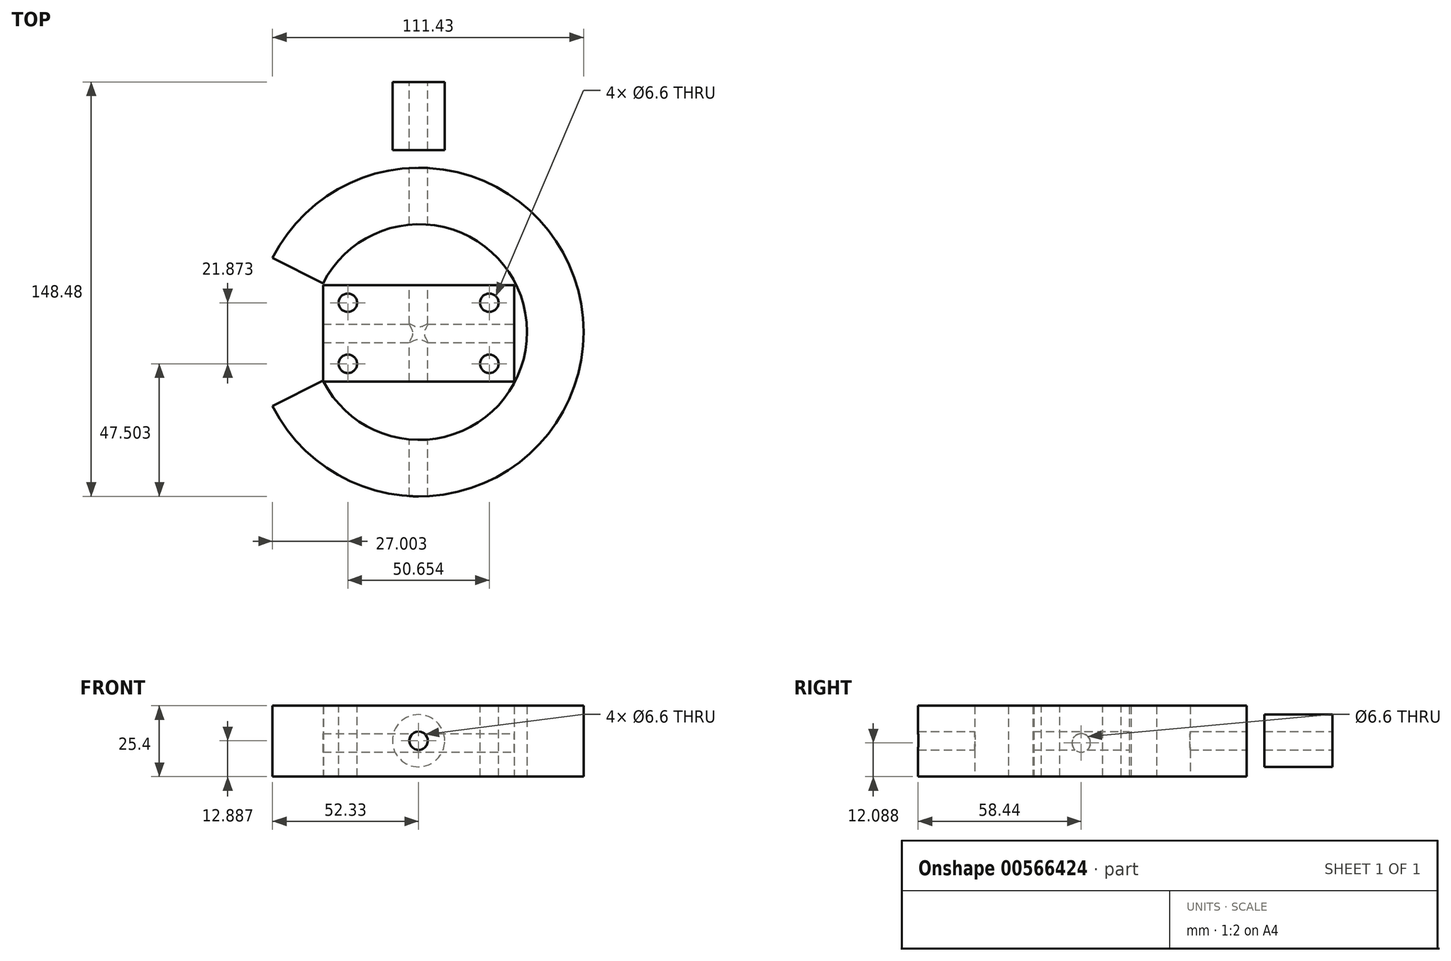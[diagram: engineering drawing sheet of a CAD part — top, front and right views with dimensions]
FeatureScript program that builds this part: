
annotation { "Feature Type Name" : "Feature", "Feature Type Description" : "" }
export const myFeature = defineFeature(function(context is Context, id is Id, definition is map)
    precondition{}
    {
        {
            var Q0;
            Q0=qCreatedBy(makeId("Top.planeOp"),FACE);
            var sketch = newSketch(context, id + "F0", { "sketchPlane" : qUnion([Q0])});
            skLineSegment(sketch, "E0.bottom", {"start": v(-34.25, 17.27) * mm, "end": v(34.25, 17.27) * mm});
            skLineSegment(sketch, "E0.top", {"start": v(-34.25, -17.27) * mm, "end": v(34.25, -17.27) * mm});
            skLineSegment(sketch, "E0.left", {"start": v(-34.25, 17.27) * mm, "end": v(-34.25, -17.27) * mm});
            skLineSegment(sketch, "E0.right", {"start": v(34.25, 17.27) * mm, "end": v(34.25, -17.27) * mm});
            skPoint(sketch, "E0.middle", {"position": v(0, 0) * mm});
            skSolve(sketch);
        }
        {
            var Q0;
            Q0=makeQuery(id+"F0.imprint","IMPRINT",FACE,{"disambiguationData":[TD([[makeQuery(id+"F0.imprint","IMPRINT",EDGE,{"derivedFrom":sQuery(id+"F0.wireOp",EDGE,"E0.bottom")}),-1.0]])]});
            extrude(context, id + "F1", {"entities" : qUnion([Q0]), "depth" : 25.4 * mm, "offsetDistance" : 25.4 * mm});
        }
        {
            var Q0;
            Q0=makeQuery(id+"F1.opExtrude","CAP_FACE",FACE,{"disambiguationData":[OSD([sQuery(id+"F0.wireOp",EDGE,"E0.bottom"),sQuery(id+"F0.wireOp",EDGE,"E0.top"),sQuery(id+"F0.wireOp",EDGE,"E0.left"),sQuery(id+"F0.wireOp",EDGE,"E0.right")])],"isStart":false});
            var sketch = newSketch(context, id + "F2", { "sketchPlane" : qUnion([Q0])});
            skPoint(sketch, "E1", {"position": v(-25.33, 10.94) * mm});
            skPoint(sketch, "E2.MirrorP", {"position": v(25.33, 10.94) * mm});
            skPoint(sketch, "E3.MirrorP", {"position": v(25.33, -10.94) * mm});
            skPoint(sketch, "E4.MirrorP", {"position": v(-25.33, -10.94) * mm});
            skSolve(sketch);
        }
        {
            var Q0;
            Q0=sQuery(id+"F2.wireOp",VERTEX,"E1");
            var Q1;
            Q1=sQuery(id+"F2.wireOp",VERTEX,"E2.MirrorP");
            var Q2;
            Q2=sQuery(id+"F2.wireOp",VERTEX,"E3.MirrorP");
            var Q3;
            Q3=sQuery(id+"F2.wireOp",VERTEX,"E4.MirrorP");
            var Q4;
            Q4=makeQuery(id+"F1.opExtrude","SWEPT_BODY",BODY,{"disambiguationData":[OSD([sQuery(id+"F0.wireOp",EDGE,"E0.bottom"),sQuery(id+"F0.wireOp",EDGE,"E0.top"),sQuery(id+"F0.wireOp",EDGE,"E0.left"),sQuery(id+"F0.wireOp",EDGE,"E0.right")])]});
            hole(context, id + "F3", {"style" : HoleStyle.SIMPLE, "endStyle" : HoleEndStyle.THROUGH, "standardTappedOrClearance" : lookupTablePath({ "standard" : "ISO", "fit" : "Normal", "size" : "M6", "type" : "Clearance" }), "standardBlindInLast" : lookupTablePath({ "fit" : "Standard", "standard" : "ISO", "size" : "M6", "type" : "Clearance" }), "holeDiameter" : 6.6 * mm, "isTappedThrough" : true, "tappedDepth" : 12.7 * mm, "tapClearance" : 3, "startFromSketch" : true, "locations" : qUnion([Q0, Q1, Q2, Q3]), "scope" : qUnion([Q4])});
        }
        {
            var Q0;
            Q0=makeQuery(id+"F1.opExtrude","SWEPT_FACE",FACE,{"disambiguationData":[OSD([sQuery(id+"F0.wireOp",EDGE,"E0.right")])]});
            var sketch = newSketch(context, id + "F4", { "sketchPlane" : qUnion([Q0])});
            skPoint(sketch, "E5", {"position": v(0, 12.09) * mm});
            skSolve(sketch);
        }
        {
            var Q0;
            Q0=sQuery(id+"F4.wireOp",VERTEX,"E5");
            var Q1;
            Q1=makeQuery(id+"F1.opExtrude","SWEPT_BODY",BODY,{"disambiguationData":[OSD([sQuery(id+"F0.wireOp",EDGE,"E0.bottom"),sQuery(id+"F0.wireOp",EDGE,"E0.top"),sQuery(id+"F0.wireOp",EDGE,"E0.left"),sQuery(id+"F0.wireOp",EDGE,"E0.right")])]});
            hole(context, id + "F5", {"style" : HoleStyle.SIMPLE, "endStyle" : HoleEndStyle.THROUGH, "standardTappedOrClearance" : lookupTablePath({ "standard" : "ISO", "fit" : "Normal", "size" : "M6", "type" : "Clearance" }), "standardBlindInLast" : lookupTablePath({ "fit" : "Standard", "standard" : "ISO", "size" : "M6", "type" : "Clearance" }), "holeDiameter" : 6.6 * mm, "isTappedThrough" : true, "tappedDepth" : 12.7 * mm, "tapClearance" : 3, "startFromSketch" : true, "locations" : qUnion([Q0]), "scope" : qUnion([Q1])});
        }
        {
            var Q0;
            Q0=qCreatedBy(makeId("Top.planeOp"),FACE);
            var sketch = newSketch(context, id + "F6", { "sketchPlane" : qUnion([Q0])});
            skArc(sketch, "E6", {"start": v(-34.25, -16.98) * mm, "mid": v(38.85, 0.43) * mm, "end": v(-34.25, 17.84) * mm});
            skArc(sketch, "E7.0", {"start": v(-52.33, -26.11) * mm, "mid": v(59.1, 0.43) * mm, "end": v(-52.33, 26.97) * mm});
            skLineSegment(sketch, "E8", {"start": v(-52.33, -26.11) * mm, "end": v(-34.25, -16.98) * mm});
            skLineSegment(sketch, "E9", {"start": v(-52.33, 26.97) * mm, "end": v(-34.25, 17.84) * mm});
            skSolve(sketch);
        }
        {
            var Q0;
            Q0=makeQuery(id+"F6.imprint","IMPRINT",FACE,{"disambiguationData":[TD([[makeQuery(id+"F6.imprint","IMPRINT",EDGE,{"derivedFrom":sQuery(id+"F6.wireOp",EDGE,"E6")}),-1.0]])]});
            extrude(context, id + "F7", {"entities" : qUnion([Q0]), "operationType" : NewBodyOperationType.ADD, "depth" : 25.4 * mm, "offsetDistance" : 25.4 * mm});
        }
        {
            var Q0;
            Q0=qCreatedBy(makeId("Right.planeOp"),FACE);
            var sketch = newSketch(context, id + "F8", { "sketchPlane" : qUnion([Q0])});
            skLineSegment(sketch, "E10.bottom", {"start": v(65.6, 22.25) * mm, "end": v(90.04, 22.25) * mm});
            skLineSegment(sketch, "E10.top", {"start": v(65.6, 3.53) * mm, "end": v(90.04, 3.53) * mm});
            skLineSegment(sketch, "E10.left", {"start": v(65.6, 3.53) * mm, "end": v(65.6, 22.25) * mm});
            skLineSegment(sketch, "E10.right", {"start": v(90.04, 3.53) * mm, "end": v(90.04, 22.25) * mm});
            skPoint(sketch, "E10.middle", {"position": v(77.82, 12.89) * mm});
            skLineSegment(sketch, "E11", {"start": v(90.04, 12.89) * mm, "end": v(65.6, 12.89) * mm});
            skSolve(sketch);
        }
        {
            var Q0;
            {var subQ0=sQuery(id+"F8.wireOp",EDGE,"E10.bottom");Q0=makeQuery(id+"F8.imprint","IMPRINT",FACE,{"disambiguationData":[TD([[makeQuery(id+"F8.imprint","IMPRINT",EDGE,{"derivedFrom":subQ0}),-1.0]])]});}
            var Q1;
            Q1=sQuery(id+"F8.wireOp",EDGE,"E11");
            revolve(context, id + "F9", {"entities" : qUnion([Q0]), "axis" : qUnion([Q1]), "revolveType" : RevolveType.FULL});
        }
        {
            var Q0;
            Q0=makeQuery(id+"F9.opRevolve","SWEPT_FACE",FACE,{"disambiguationData":[OSD([sQuery(id+"F8.wireOp",EDGE,"E10.right")])]});
            var sketch = newSketch(context, id + "F10", { "sketchPlane" : qUnion([Q0])});
            skPoint(sketch, "E12", {"position": v(0, 12.89) * mm});
            skSolve(sketch);
        }
        {
            var Q0;
            Q0=sQuery(id+"F10.wireOp",VERTEX,"E12");
            var Q1;
            Q1=makeQuery(id+"F1.opExtrude","SWEPT_BODY",BODY,{"disambiguationData":[OSD([sQuery(id+"F0.wireOp",EDGE,"E0.bottom"),sQuery(id+"F0.wireOp",EDGE,"E0.top"),sQuery(id+"F0.wireOp",EDGE,"E0.left"),sQuery(id+"F0.wireOp",EDGE,"E0.right")])]});
            var Q2;
            Q2=makeQuery(id+"F9.opRevolve","SWEPT_BODY",BODY,{"disambiguationData":[OSD([sQuery(id+"F8.wireOp",EDGE,"E10.bottom"),sQuery(id+"F8.wireOp",EDGE,"E10.left"),sQuery(id+"F8.wireOp",EDGE,"E10.right"),sQuery(id+"F8.wireOp",EDGE,"E11")])]});
            hole(context, id + "F11", {"style" : HoleStyle.SIMPLE, "endStyle" : HoleEndStyle.THROUGH, "standardTappedOrClearance" : lookupTablePath({ "standard" : "ISO", "fit" : "Normal", "size" : "M6", "type" : "Clearance" }), "standardBlindInLast" : lookupTablePath({ "fit" : "Standard", "standard" : "ISO", "size" : "M6", "type" : "Clearance" }), "holeDiameter" : 6.6 * mm, "isTappedThrough" : true, "tappedDepth" : 12.7 * mm, "tapClearance" : 3, "startFromSketch" : true, "locations" : qUnion([Q0]), "scope" : qUnion([Q1, Q2])});
        }
    });
